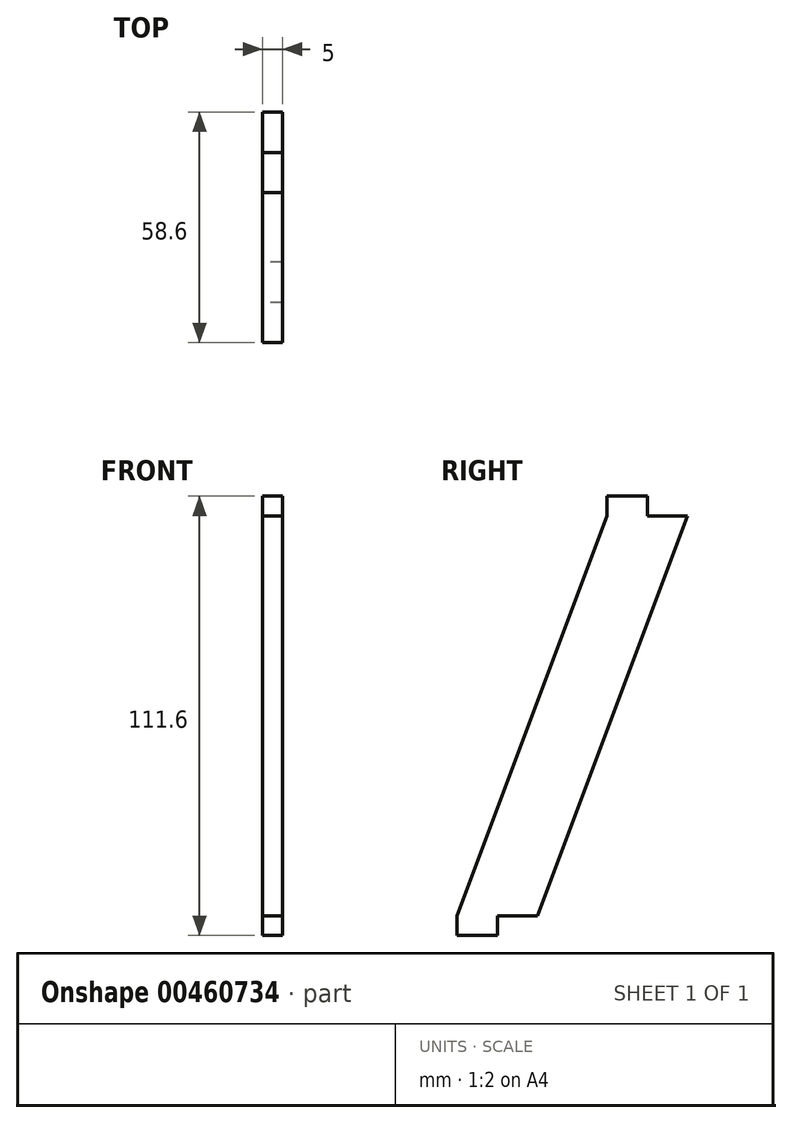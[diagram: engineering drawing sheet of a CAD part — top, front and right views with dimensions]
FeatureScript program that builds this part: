
annotation { "Feature Type Name" : "Feature", "Feature Type Description" : "" }
export const myFeature = defineFeature(function(context is Context, id is Id, definition is map)
    precondition{}
    {
        {
            var Q0;
            Q0=qCreatedBy(makeId("Right.planeOp"),FACE);
            var sketch = newSketch(context, id + "F0", { "sketchPlane" : qUnion([Q0])});
            skLineSegment(sketch, "E0", {"start": v(0, 0) * mm, "end": v(-38.1, -101.6) * mm});
            skLineSegment(sketch, "E1", {"start": v(-38.1, -101.6) * mm, "end": v(-48.35, -101.6) * mm});
            skLineSegment(sketch, "E2", {"start": v(-48.35, -101.6) * mm, "end": v(-48.35, -106.6) * mm});
            skLineSegment(sketch, "E3", {"start": v(-48.35, -106.6) * mm, "end": v(-58.6, -106.6) * mm});
            skLineSegment(sketch, "E4", {"start": v(-58.6, -106.6) * mm, "end": v(-58.6, -101.6) * mm});
            skLineSegment(sketch, "E5", {"start": v(-58.6, -101.6) * mm, "end": v(-20.5, 0) * mm});
            skLineSegment(sketch, "E6", {"start": v(-20.5, 0) * mm, "end": v(-20.5, 5) * mm});
            skLineSegment(sketch, "E7", {"start": v(-20.5, 5) * mm, "end": v(-10.25, 5) * mm});
            skLineSegment(sketch, "E8", {"start": v(-10.25, 5) * mm, "end": v(-10.25, 0) * mm});
            skLineSegment(sketch, "E9", {"start": v(-10.25, 0) * mm, "end": v(0, 0) * mm});
            skPoint(sketch, "E10", {"position": v(-38.1, -101.6) * mm});
            skPoint(sketch, "E11", {"position": v(0, -101.6) * mm});
            skPoint(sketch, "E12", {"position": v(-58.6, -106.6) * mm});
            skPoint(sketch, "E13", {"position": v(0, 5) * mm});
            skPoint(sketch, "E14", {"position": v(0, -106.6) * mm});
            skPoint(sketch, "E15", {"position": v(67.5, 0) * mm});
            skPoint(sketch, "E16", {"position": v(67.5, -101.01) * mm});
            skSolve(sketch);
        }
        {
            var Q0;
            Q0=makeQuery(id+"F0.imprint","IMPRINT",FACE,{"disambiguationData":[TD([[makeQuery(id+"F0.imprint","IMPRINT",EDGE,{"derivedFrom":sQuery(id+"F0.wireOp",EDGE,"E0")}),-1.0]])]});
            extrude(context, id + "F1", {"entities" : qUnion([Q0]), "depth" : 5 * mm});
        }
    });
